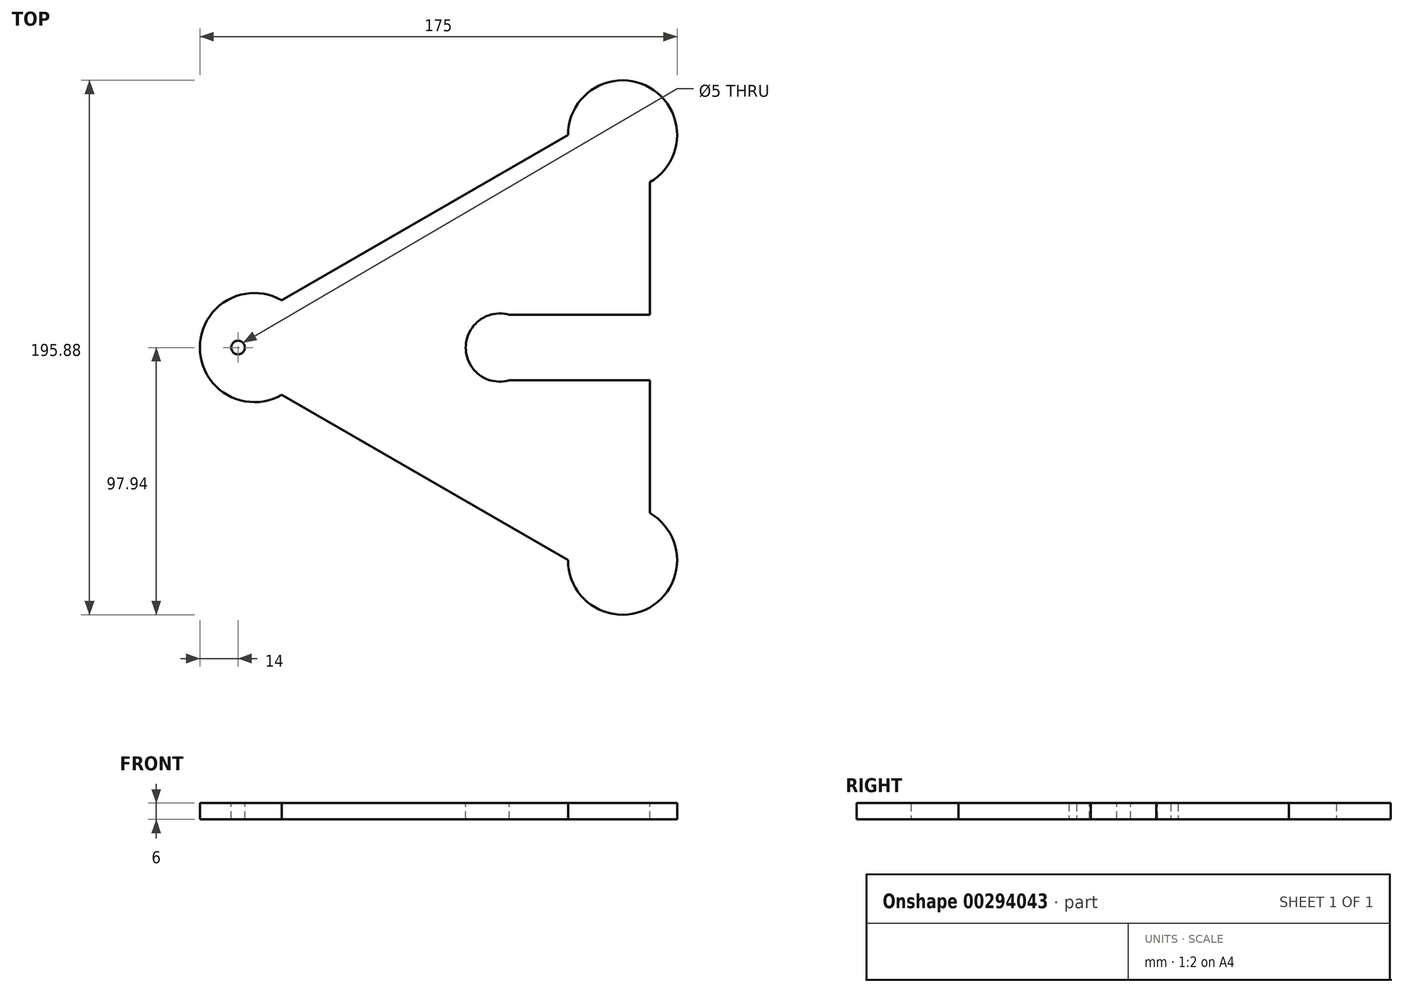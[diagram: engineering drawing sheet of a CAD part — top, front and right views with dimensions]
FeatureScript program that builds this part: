
annotation { "Feature Type Name" : "Feature", "Feature Type Description" : "" }
export const myFeature = defineFeature(function(context is Context, id is Id, definition is map)
    precondition{}
    {
        {
            var Q0;
            Q0=qCreatedBy(makeId("Top.planeOp"),FACE);
            var sketch = newSketch(context, id + "F0", { "sketchPlane" : qUnion([Q0])});
            skCircle(sketch, "E0.cCircle", {"center": v(0, 0) * mm, "radius": 110 * mm, "construction": true});
            skLineSegment(sketch, "E0.0", {"start": v(-110, 0) * mm, "end": v(55, 95.26) * mm});
            skLineSegment(sketch, "E0.1", {"start": v(55, 95.26) * mm, "end": v(55, -95.26) * mm});
            skLineSegment(sketch, "E0.2", {"start": v(55, -95.26) * mm, "end": v(-110, 0) * mm});
            skLineSegment(sketch, "E1", {"start": v(-110, 0) * mm, "end": v(55, 0) * mm, "construction": true});
            skCircle(sketch, "E2", {"center": v(-90, 0) * mm, "radius": 20 * mm});
            skCircle(sketch, "E3.1.0", {"center": v(45, -77.94) * mm, "radius": 20 * mm});
            skCircle(sketch, "E3.2.0", {"center": v(45, 77.94) * mm, "radius": 20 * mm});
            skSolve(sketch);
        }
        {
            var Q0;
            Q0 = qSketchRegion(id + "F0", true);
            extrude(context, id + "F1", {"entities" : qUnion([Q0]), "depth" : 6 * mm, "offsetDistance" : 25 * mm});
        }
        {
            var Q0;
            Q0=makeQuery(id+"F1.opExtrude","CAP_FACE",FACE,{"disambiguationData":[OSD([sQuery(id+"F0.wireOp",EDGE,"E0.0"),sQuery(id+"F0.wireOp",EDGE,"E0.1"),sQuery(id+"F0.wireOp",EDGE,"E0.2"),sQuery(id+"F0.wireOp",EDGE,"E2"),sQuery(id+"F0.wireOp",EDGE,"E3.1.0"),sQuery(id+"F0.wireOp",EDGE,"E3.2.0")])],"isStart":false});
            var sketch = newSketch(context, id + "F2", { "sketchPlane" : qUnion([Q0])});
            skCircle(sketch, "E4", {"center": v(0, 0) * mm, "radius": 12.5 * mm});
            skSolve(sketch);
        }
        {
            var Q0;
            Q0 = qSketchRegion(id + "F2", true);
            extrude(context, id + "F3", {"entities" : qUnion([Q0]), "operationType" : NewBodyOperationType.REMOVE, "endBound" : BoundingType.UP_TO_NEXT, "oppositeDirection" : true, "depth" : 25 * mm, "offsetDistance" : 25 * mm});
        }
        {
            var Q0;
            Q0=makeQuery(id+"F1.opExtrude","CAP_FACE",FACE,{"disambiguationData":[OSD([sQuery(id+"F0.wireOp",EDGE,"E0.0"),sQuery(id+"F0.wireOp",EDGE,"E0.1"),sQuery(id+"F0.wireOp",EDGE,"E0.2"),sQuery(id+"F0.wireOp",EDGE,"E2"),sQuery(id+"F0.wireOp",EDGE,"E3.1.0"),sQuery(id+"F0.wireOp",EDGE,"E3.2.0")])],"isStart":false});
            var sketch = newSketch(context, id + "F4", { "sketchPlane" : qUnion([Q0])});
            skLineSegment(sketch, "E5", {"start": v(0, 0) * mm, "end": v(-96, 0) * mm, "construction": true});
            skCircle(sketch, "E6", {"center": v(-96, 0) * mm, "radius": 2.5 * mm});
            skSolve(sketch);
        }
        {
            var Q0;
            Q0 = qSketchRegion(id + "F4", true);
            extrude(context, id + "F5", {"entities" : qUnion([Q0]), "operationType" : NewBodyOperationType.REMOVE, "endBound" : BoundingType.UP_TO_NEXT, "oppositeDirection" : true, "depth" : 25 * mm, "offsetDistance" : 25 * mm});
        }
        {
            var Q0;
            Q0=makeQuery(id+"F1.opExtrude","CAP_FACE",FACE,{"disambiguationData":[OSD([sQuery(id+"F0.wireOp",EDGE,"E0.0"),sQuery(id+"F0.wireOp",EDGE,"E0.1"),sQuery(id+"F0.wireOp",EDGE,"E0.2"),sQuery(id+"F0.wireOp",EDGE,"E2"),sQuery(id+"F0.wireOp",EDGE,"E3.1.0"),sQuery(id+"F0.wireOp",EDGE,"E3.2.0")])],"isStart":false});
            var sketch = newSketch(context, id + "F6", { "sketchPlane" : qUnion([Q0])});
            skLineSegment(sketch, "E7", {"start": v(0, 0) * mm, "end": v(55, 0) * mm, "construction": true});
            skLineSegment(sketch, "E8.bottom", {"start": v(3.5, -12) * mm, "end": v(63.5, -12) * mm});
            skLineSegment(sketch, "E8.top", {"start": v(3.5, 12) * mm, "end": v(63.5, 12) * mm});
            skLineSegment(sketch, "E8.left", {"start": v(3.5, -12) * mm, "end": v(3.5, 12) * mm});
            skLineSegment(sketch, "E8.right", {"start": v(63.5, -12) * mm, "end": v(63.5, 12) * mm});
            skPoint(sketch, "E8.middle", {"position": v(33.5, 0) * mm});
            skSolve(sketch);
        }
        {
            var Q0;
            Q0 = qSketchRegion(id + "F6", true);
            extrude(context, id + "F7", {"entities" : qUnion([Q0]), "operationType" : NewBodyOperationType.REMOVE, "endBound" : BoundingType.UP_TO_NEXT, "oppositeDirection" : true, "depth" : 25 * mm, "offsetDistance" : 25 * mm});
        }
    });
